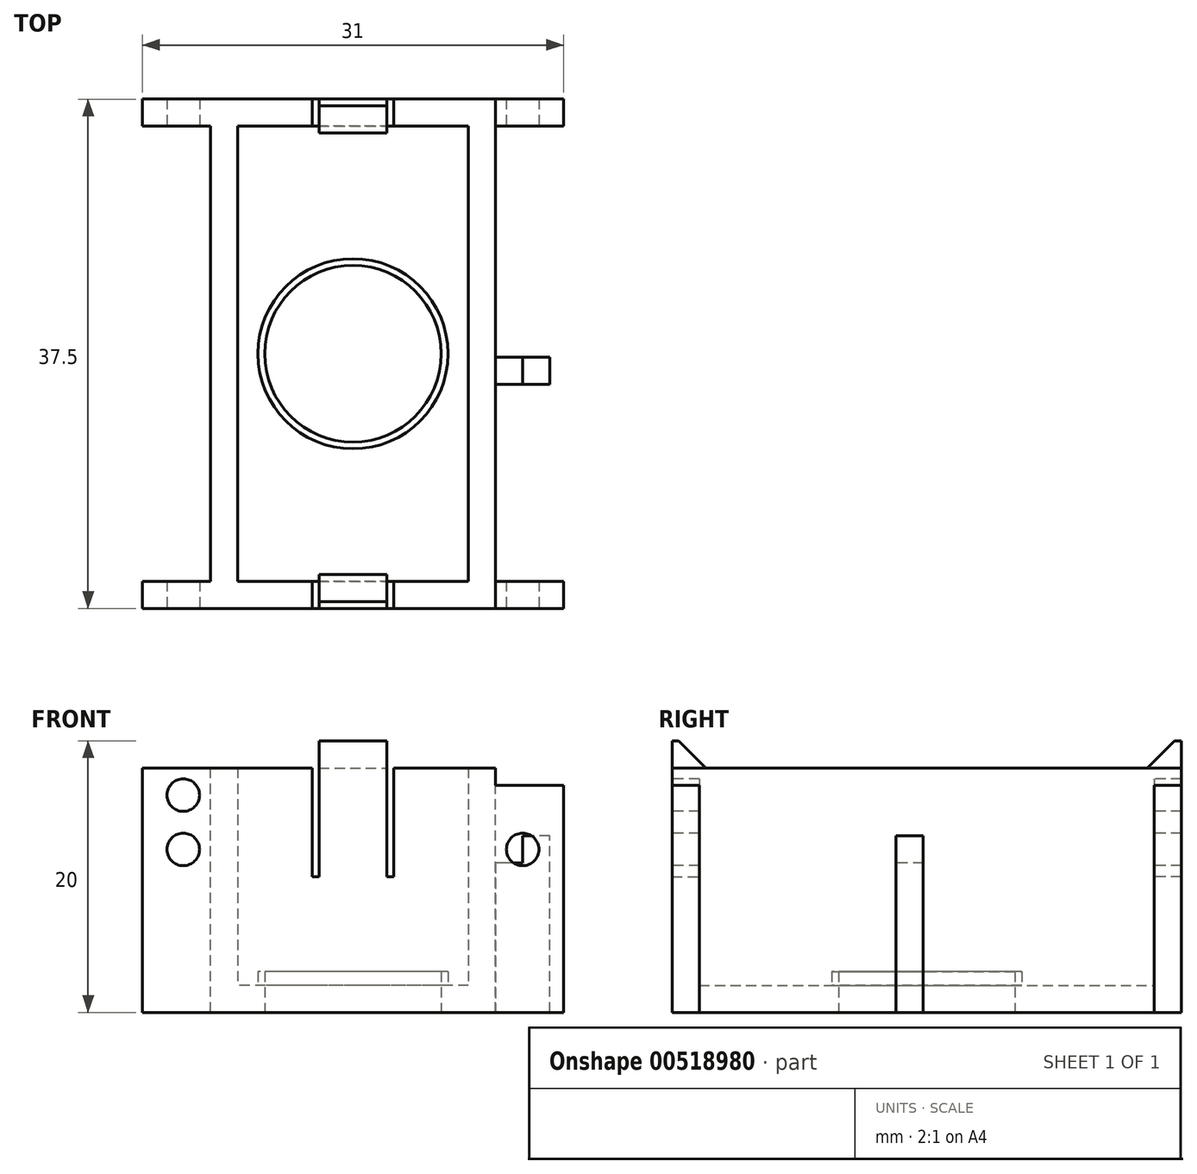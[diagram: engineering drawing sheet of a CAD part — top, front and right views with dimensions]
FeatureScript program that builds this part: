
annotation { "Feature Type Name" : "Feature", "Feature Type Description" : "" }
export const myFeature = defineFeature(function(context is Context, id is Id, definition is map)
    precondition{}
    {
        {
            var Q0;
            Q0=qCreatedBy(makeId("Top.planeOp"),FACE);
            var sketch = newSketch(context, id + "F0", { "sketchPlane" : qUnion([Q0])});
            skLineSegment(sketch, "E0.bottom", {"start": v(-9.66, 7.75) * mm, "end": v(7.34, 7.75) * mm});
            skLineSegment(sketch, "E0.top", {"start": v(-9.66, -25.75) * mm, "end": v(7.34, -25.75) * mm});
            skLineSegment(sketch, "E0.left", {"start": v(-9.66, 7.75) * mm, "end": v(-9.66, -25.75) * mm});
            skLineSegment(sketch, "E0.right", {"start": v(7.34, 7.75) * mm, "end": v(7.34, -25.75) * mm});
            skLineSegment(sketch, "E1.bottom", {"start": v(-11.66, 9.75) * mm, "end": v(9.34, 9.75) * mm});
            skLineSegment(sketch, "E1.top", {"start": v(-11.66, -27.75) * mm, "end": v(9.34, -27.75) * mm});
            skLineSegment(sketch, "E1.left", {"start": v(-11.66, 9.75) * mm, "end": v(-11.66, -27.75) * mm});
            skLineSegment(sketch, "E1.right", {"start": v(9.34, 9.75) * mm, "end": v(9.34, -27.75) * mm});
            skLineSegment(sketch, "E2", {"start": v(7.34, 0) * mm, "end": v(9.34, 0) * mm, "construction": true});
            skLineSegment(sketch, "E3", {"start": v(-9.66, 5.82) * mm, "end": v(-11.66, 5.82) * mm, "construction": true});
            skLineSegment(sketch, "E4", {"start": v(13.26, 7.75) * mm, "end": v(13.26, 9.75) * mm, "construction": true});
            skLineSegment(sketch, "E5", {"start": v(14.78, -25.75) * mm, "end": v(14.78, -27.75) * mm, "construction": true});
            skLineSegment(sketch, "E6.top", {"start": v(-9.66, -1.25) * mm, "end": v(7.34, -1.25) * mm});
            skLineSegment(sketch, "E6.left", {"start": v(-9.66, 7.75) * mm, "end": v(-9.66, -1.25) * mm});
            skLineSegment(sketch, "E6.right", {"start": v(7.34, 7.75) * mm, "end": v(7.34, -1.25) * mm});
            skLineSegment(sketch, "E7.top", {"start": v(-9.66, -16.75) * mm, "end": v(7.34, -16.75) * mm});
            skLineSegment(sketch, "E7.left", {"start": v(-9.66, -25.75) * mm, "end": v(-9.66, -16.75) * mm});
            skLineSegment(sketch, "E7.right", {"start": v(7.34, -25.75) * mm, "end": v(7.34, -16.75) * mm});
            skCircle(sketch, "E8", {"center": v(-1.16, 1.95) * mm, "radius": 5.5 * mm});
            skCircle(sketch, "E9", {"center": v(-1.16, -19.95) * mm, "radius": 5.5 * mm});
            skLineSegment(sketch, "E10", {"start": v(-1.16, 7.75) * mm, "end": v(-1.16, 1.95) * mm, "construction": true});
            skLineSegment(sketch, "E11", {"start": v(-1.16, -25.75) * mm, "end": v(-1.16, -19.95) * mm, "construction": true});
            skLineSegment(sketch, "E12.bottom", {"start": v(-5.16, 9.75) * mm, "end": v(2.84, 9.75) * mm});
            skLineSegment(sketch, "E13.bottom", {"start": v(-5.16, -27.75) * mm, "end": v(2.84, -27.75) * mm});
            skLineSegment(sketch, "E13.left", {"start": v(-5.16, -27.75) * mm, "end": v(-5.16, -35.75) * mm});
            skLineSegment(sketch, "E13.right", {"start": v(2.84, -27.75) * mm, "end": v(2.84, -35.75) * mm});
            skCircle(sketch, "E14", {"center": v(-1.16, 13.5) * mm, "radius": 1.7 * mm});
            skLineSegment(sketch, "E15", {"start": v(-1.16, -31.5) * mm, "end": v(-1.16, -27.75) * mm, "construction": true});
            skLineSegment(sketch, "E16", {"start": v(-1.16, 13.5) * mm, "end": v(-1.16, 9.75) * mm, "construction": true});
            skCircle(sketch, "E17", {"center": v(-1.16, -9) * mm, "radius": 6.5 * mm});
            skPoint(sketch, "E17.centerSnap0", {"position": v(-1.16, -1.25) * mm});
            skLineSegment(sketch, "E18", {"start": v(-1.16, -9) * mm, "end": v(-1.16, 1.95) * mm, "construction": true});
            skLineSegment(sketch, "E19", {"start": v(-1.16, -9) * mm, "end": v(-1.16, -19.95) * mm, "construction": true});
            skCircle(sketch, "E20", {"center": v(-1.16, -9) * mm, "radius": 7 * mm});
            skSolve(sketch);
        }
        {
            var Q0;
            Q0=makeQuery(id+"F0.imprint","IMPRINT",FACE,{"disambiguationData":[TD([[makeQuery(id+"F0.imprint","IMPRINT",EDGE,{"derivedFrom":sQuery(id+"F0.wireOp",EDGE,"E0.left")}),-1.0]])]});
            var Q1;
            Q1=makeQuery(id+"F0.imprint","IMPRINT",FACE,{"disambiguationData":[TD([[makeQuery(id+"F0.imprint","IMPRINT",EDGE,{"derivedFrom":sQuery(id+"F0.wireOp",EDGE,"E0.bottom")}),-1.0]])]});
            var Q2;
            Q2=makeQuery(id+"F0.imprint","IMPRINT",FACE,{"disambiguationData":[TD([[makeQuery(id+"F0.imprint","IMPRINT",EDGE,{"derivedFrom":sQuery(id+"F0.wireOp",EDGE,"E0.top")}),1.0]])]});
            var Q3;
            Q3=makeQuery(id+"F0.imprint","IMPRINT",FACE,{"disambiguationData":[TD([[makeQuery(id+"F0.imprint","IMPRINT",EDGE,{"derivedFrom":sQuery(id+"F0.wireOp",EDGE,"E12.bottom")}),1.0]])]});
            var Q4;
            Q4=makeQuery(id+"F0.imprint","IMPRINT",FACE,{"disambiguationData":[TD([[makeQuery(id+"F0.imprint","IMPRINT",EDGE,{"derivedFrom":sQuery(id+"F0.wireOp",EDGE,"E13.bottom")}),-1.0]])]});
            var Q5;
            {var subQ0=sQuery(id+"F0.wireOp",EDGE,"E9");var subQ1=sQuery(id+"F0.wireOp",EDGE,"E7.top");var subQ2=makeQuery(id+"F0.imprint","INTERSECT",VERTEX,{"disambiguationData":[OD(0.0)],"derivedFrom":[subQ1,subQ0]});Q5=makeQuery(id+"F0.imprint","IMPRINT",FACE,{"disambiguationData":[TD([[makeQuery(id+"F0.imprint","IMPRINT",EDGE,{"disambiguationData":[TD([[subQ2,-1.0]])],"derivedFrom":subQ1}),-1.0]])]});}
            var Q6;
            {var subQ0=sQuery(id+"F0.wireOp",EDGE,"E8");var subQ1=sQuery(id+"F0.wireOp",EDGE,"E6.top");var subQ2=makeQuery(id+"F0.imprint","INTERSECT",VERTEX,{"disambiguationData":[OD(0.0)],"derivedFrom":[subQ1,subQ0]});Q6=makeQuery(id+"F0.imprint","IMPRINT",FACE,{"disambiguationData":[TD([[makeQuery(id+"F0.imprint","IMPRINT",EDGE,{"disambiguationData":[TD([[subQ2,-1.0]])],"derivedFrom":subQ1}),1.0]])]});}
            var Q7;
            {var subQ6=sQuery(id+"F0.wireOp",EDGE,"E0.right");Q7=makeQuery(id+"F0.imprint","IMPRINT",FACE,{"disambiguationData":[TD([[makeQuery(id+"F0.imprint","IMPRINT",EDGE,{"derivedFrom":subQ6}),-1.0]])]});}
            var Q8;
            {var subQ0=sQuery(id+"F0.wireOp",EDGE,"E8");var subQ1=sQuery(id+"F0.wireOp",EDGE,"E6.top");var subQ2=makeQuery(id+"F0.imprint","INTERSECT",VERTEX,{"disambiguationData":[OD(0.0)],"derivedFrom":[subQ1,subQ0]});Q8=makeQuery(id+"F0.imprint","IMPRINT",FACE,{"disambiguationData":[TD([[makeQuery(id+"F0.imprint","IMPRINT",EDGE,{"disambiguationData":[TD([[subQ2,-1.0]])],"derivedFrom":subQ1}),-1.0]])]});}
            var Q9;
            {var subQ1=sQuery(id+"F0.wireOp",EDGE,"E0.left");Q9=makeQuery(id+"F0.imprint","IMPRINT",FACE,{"disambiguationData":[TD([[makeQuery(id+"F0.imprint","IMPRINT",EDGE,{"derivedFrom":subQ1}),1.0]])]});}
            var Q10;
            {var subQ0=sQuery(id+"F0.wireOp",EDGE,"E9");var subQ1=sQuery(id+"F0.wireOp",EDGE,"E7.top");var subQ2=makeQuery(id+"F0.imprint","INTERSECT",VERTEX,{"disambiguationData":[OD(0.0)],"derivedFrom":[subQ1,subQ0]});Q10=makeQuery(id+"F0.imprint","IMPRINT",FACE,{"disambiguationData":[TD([[makeQuery(id+"F0.imprint","IMPRINT",EDGE,{"disambiguationData":[TD([[subQ2,-1.0]])],"derivedFrom":subQ1}),1.0]])]});}
            extrude(context, id + "F1", {"entities" : qUnion([Q0, Q1, Q2, Q3, Q4, Q5, Q6, Q7, Q8, Q9, Q10]), "depth" : 2 * mm, "offsetDistance" : 25 * mm});
        }
        {
            var Q0;
            Q0=makeQuery(id+"F0.imprint","IMPRINT",FACE,{"disambiguationData":[TD([[makeQuery(id+"F0.imprint","IMPRINT",EDGE,{"derivedFrom":sQuery(id+"F0.wireOp",EDGE,"E0.left")}),-1.0]])]});
            extrude(context, id + "F2", {"entities" : qUnion([Q0]), "operationType" : NewBodyOperationType.ADD, "depth" : 9 * mm + 9 * mm, "offsetDistance" : 25 * mm});
        }
        {
            var Q0;
            {var subQ0=sQuery(id+"F0.wireOp",EDGE,"E20");var subQ1=sQuery(id+"F0.wireOp",EDGE,"E8");var subQ2=makeQuery(id+"F0.imprint","INTERSECT",VERTEX,{"disambiguationData":[OD(0.0)],"derivedFrom":[subQ1,subQ0]});Q0=makeQuery(id+"F0.imprint","IMPRINT",FACE,{"disambiguationData":[TD([[makeQuery(id+"F0.imprint","IMPRINT",EDGE,{"disambiguationData":[TD([[subQ2,-1.0]])],"derivedFrom":subQ1}),-1.0]])]});}
            var Q1;
            {var subQ0=sQuery(id+"F0.wireOp",EDGE,"E20");var subQ1=sQuery(id+"F0.wireOp",EDGE,"E8");var subQ2=makeQuery(id+"F0.imprint","INTERSECT",VERTEX,{"disambiguationData":[OD(0.0)],"derivedFrom":[subQ1,subQ0]});Q1=makeQuery(id+"F0.imprint","IMPRINT",FACE,{"disambiguationData":[TD([[makeQuery(id+"F0.imprint","IMPRINT",EDGE,{"disambiguationData":[TD([[subQ2,-1.0]])],"derivedFrom":subQ1}),1.0]])]});}
            var Q2;
            {var subQ0=sQuery(id+"F0.wireOp",EDGE,"E17");var subQ1=sQuery(id+"F0.wireOp",EDGE,"E8");var subQ2=makeQuery(id+"F0.imprint","INTERSECT",VERTEX,{"disambiguationData":[OD(1.0)],"derivedFrom":[subQ1,subQ0]});Q2=makeQuery(id+"F0.imprint","IMPRINT",FACE,{"disambiguationData":[TD([[makeQuery(id+"F0.imprint","IMPRINT",EDGE,{"disambiguationData":[TD([[subQ2,-1.0]])],"derivedFrom":subQ1}),-1.0]])]});}
            var Q3;
            {var subQ0=sQuery(id+"F0.wireOp",EDGE,"E20");var subQ1=sQuery(id+"F0.wireOp",EDGE,"E9");var subQ2=makeQuery(id+"F0.imprint","INTERSECT",VERTEX,{"disambiguationData":[OD(0.0)],"derivedFrom":[subQ1,subQ0]});Q3=makeQuery(id+"F0.imprint","IMPRINT",FACE,{"disambiguationData":[TD([[makeQuery(id+"F0.imprint","IMPRINT",EDGE,{"disambiguationData":[TD([[subQ2,-1.0]])],"derivedFrom":subQ1}),1.0]])]});}
            extrude(context, id + "F3", {"entities" : qUnion([Q0, Q1, Q2, Q3]), "operationType" : NewBodyOperationType.ADD, "depth" : 3 * mm, "offsetDistance" : 25 * mm});
        }
        {
            var Q0;
            {var subQ0=sQuery(id+"F0.wireOp",EDGE,"E1.left");Q0=makeQuery(id+"F2.boolean.opBoolean","MERGE",FACE,{"derivedFrom":[makeQuery(id+"F1.opExtrude","SWEPT_FACE",FACE,{"disambiguationData":[OSD([subQ0])]}),makeQuery(id+"F2.opExtrude","SWEPT_FACE",FACE,{"disambiguationData":[OSD([subQ0])]})]});}
            var sketch = newSketch(context, id + "F4", { "sketchPlane" : qUnion([Q0])});
            skLineSegment(sketch, "E21.bottom", {"start": v(-9.75, 0) * mm, "end": v(-7.75, 0) * mm});
            skLineSegment(sketch, "E21.top", {"start": v(-9.75, 5) * mm, "end": v(-7.75, 5) * mm});
            skLineSegment(sketch, "E21.left", {"start": v(-9.75, 0) * mm, "end": v(-9.75, 5) * mm});
            skLineSegment(sketch, "E21.right", {"start": v(-7.75, 0) * mm, "end": v(-7.75, 5) * mm});
            skLineSegment(sketch, "E22.bottom", {"start": v(27.75, 0) * mm, "end": v(25.75, 0) * mm});
            skLineSegment(sketch, "E22.top", {"start": v(27.75, 5) * mm, "end": v(25.75, 5) * mm});
            skLineSegment(sketch, "E22.left", {"start": v(27.75, 0) * mm, "end": v(27.75, 5) * mm});
            skLineSegment(sketch, "E22.right", {"start": v(25.75, 0) * mm, "end": v(25.75, 5) * mm});
            skLineSegment(sketch, "E23.bottom", {"start": v(-9.75, 18) * mm, "end": v(-7.75, 18) * mm});
            skLineSegment(sketch, "E23.left", {"start": v(-9.75, 18) * mm, "end": v(-9.75, 5) * mm});
            skLineSegment(sketch, "E23.right", {"start": v(-7.75, 18) * mm, "end": v(-7.75, 5) * mm});
            skLineSegment(sketch, "E24.bottom", {"start": v(25.75, 5) * mm, "end": v(27.75, 5) * mm});
            skLineSegment(sketch, "E24.top", {"start": v(25.75, 18) * mm, "end": v(27.75, 18) * mm});
            skLineSegment(sketch, "E24.left", {"start": v(25.75, 5) * mm, "end": v(25.75, 18) * mm});
            skLineSegment(sketch, "E24.right", {"start": v(27.75, 5) * mm, "end": v(27.75, 18) * mm});
            skSolve(sketch);
        }
        {
            var Q0;
            Q0=qSketchRegion(id+"F4",true);
            extrude(context, id + "F5", {"entities" : qUnion([Q0]), "operationType" : NewBodyOperationType.ADD, "depth" : 5 * mm, "offsetDistance" : 25 * mm});
        }
        {
            var Q0;
            {var subQ0=sQuery(id+"F0.wireOp",EDGE,"E1.right");Q0=makeQuery(id+"F2.boolean.opBoolean","MERGE",FACE,{"derivedFrom":[makeQuery(id+"F1.opExtrude","SWEPT_FACE",FACE,{"disambiguationData":[OSD([subQ0])]}),makeQuery(id+"F2.opExtrude","SWEPT_FACE",FACE,{"disambiguationData":[OSD([subQ0])]})]});}
            var sketch = newSketch(context, id + "F6", { "sketchPlane" : qUnion([Q0])});
            skLineSegment(sketch, "E25.bottom", {"start": v(-27.75, 0) * mm, "end": v(-25.75, 0) * mm});
            skLineSegment(sketch, "E25.top", {"start": v(-27.75, 16.72) * mm, "end": v(-25.75, 16.72) * mm});
            skLineSegment(sketch, "E25.left", {"start": v(-27.75, 0) * mm, "end": v(-27.75, 16.72) * mm});
            skLineSegment(sketch, "E25.right", {"start": v(-25.75, 0) * mm, "end": v(-25.75, 16.72) * mm});
            skLineSegment(sketch, "E26.bottom", {"start": v(9.75, 0) * mm, "end": v(7.75, 0) * mm});
            skLineSegment(sketch, "E26.top", {"start": v(9.75, 16.72) * mm, "end": v(7.75, 16.72) * mm});
            skLineSegment(sketch, "E26.left", {"start": v(9.75, 0) * mm, "end": v(9.75, 16.72) * mm});
            skLineSegment(sketch, "E26.right", {"start": v(7.75, 0) * mm, "end": v(7.75, 16.72) * mm});
            skSolve(sketch);
        }
        {
            var Q0;
            Q0=qSketchRegion(id+"F6",true);
            extrude(context, id + "F7", {"entities" : qUnion([Q0]), "operationType" : NewBodyOperationType.ADD, "depth" : 5 * mm, "offsetDistance" : 25 * mm});
        }
        {
            var Q0;
            {var subQ0=sQuery(id+"F0.wireOp",EDGE,"E13.bottom");var subQ1=sQuery(id+"F0.wireOp",EDGE,"E1.top");Q0=makeQuery(id+"F7.boolean.opBoolean","MERGE",FACE,{"derivedFrom":[makeQuery(id+"F5.boolean.opBoolean","MERGE",FACE,{"derivedFrom":[makeQuery(id+"F2.boolean.opBoolean","MERGE",FACE,{"derivedFrom":[makeQuery(id+"F1.opExtrude","SWEPT_FACE",FACE,{"disambiguationData":[OSD([subQ1,subQ0])]}),makeQuery(id+"F2.opExtrude","SWEPT_FACE",FACE,{"disambiguationData":[OSD([subQ1,subQ0])]})]}),makeQuery(id+"F5.opExtrude","SWEPT_FACE",FACE,{"disambiguationData":[OSD([sQuery(id+"F4.wireOp",EDGE,"E22.left")])]})]}),makeQuery(id+"F7.opExtrude","SWEPT_FACE",FACE,{"disambiguationData":[OSD([sQuery(id+"F6.wireOp",EDGE,"E25.left")])]})]});}
            var sketch = newSketch(context, id + "F8", { "sketchPlane" : qUnion([Q0])});
            skCircle(sketch, "E27", {"center": v(-13.66, 12) * mm, "radius": 1.2 * mm});
            skPoint(sketch, "E27.centerSnap0", {"position": v(-13.66, 5) * mm});
            skCircle(sketch, "E28", {"center": v(11.34, 12) * mm, "radius": 1.2 * mm});
            skLineSegment(sketch, "E29", {"start": v(-13.66, 12) * mm, "end": v(-16.66, 12) * mm, "construction": true});
            skLineSegment(sketch, "E30", {"start": v(11.34, 12) * mm, "end": v(14.34, 12) * mm, "construction": true});
            skCircle(sketch, "E31", {"center": v(-13.66, 16) * mm, "radius": 1.2 * mm});
            skSolve(sketch);
        }
        {
            var Q0;
            Q0=qSketchRegion(id+"F8",true);
            extrude(context, id + "F9", {"entities" : qUnion([Q0]), "operationType" : NewBodyOperationType.REMOVE, "oppositeDirection" : true, "depth" : 40 * mm, "offsetDistance" : 25 * mm});
        }
        {
            var Q0;
            {var subQ0=sQuery(id+"F0.wireOp",EDGE,"E12.bottom");var subQ1=sQuery(id+"F0.wireOp",EDGE,"E1.bottom");Q0=makeQuery(id+"F7.boolean.opBoolean","MERGE",FACE,{"derivedFrom":[makeQuery(id+"F5.boolean.opBoolean","MERGE",FACE,{"derivedFrom":[makeQuery(id+"F2.boolean.opBoolean","MERGE",FACE,{"derivedFrom":[makeQuery(id+"F1.opExtrude","SWEPT_FACE",FACE,{"disambiguationData":[OSD([subQ1,subQ0])]}),makeQuery(id+"F2.opExtrude","SWEPT_FACE",FACE,{"disambiguationData":[OSD([subQ1,subQ0])]})]}),makeQuery(id+"F5.opExtrude","SWEPT_FACE",FACE,{"disambiguationData":[OSD([sQuery(id+"F4.wireOp",EDGE,"E21.left")])]})]}),makeQuery(id+"F7.opExtrude","SWEPT_FACE",FACE,{"disambiguationData":[OSD([sQuery(id+"F6.wireOp",EDGE,"E26.left")])]})]});}
            cPlane(context, id + "F10", {"entities" : qUnion([Q0]), "cplaneType" : CPlaneType.OFFSET, "offset" : 20 * mm, "oppositeDirection" : true, "width" : 150 * mm, "height" : 150 * mm});
        }
        {
            var Q0;
            Q0=qCreatedBy(id+"F10.planeOp",FACE);
            var sketch = newSketch(context, id + "F11", { "sketchPlane" : qUnion([Q0])});
            skLineSegment(sketch, "E32", {"start": v(-13.34, 0) * mm, "end": v(-13.34, 13) * mm});
            skLineSegment(sketch, "E33", {"start": v(-13.34, 13) * mm, "end": v(-11.34, 13) * mm});
            skLineSegment(sketch, "E34", {"start": v(-11.34, 13) * mm, "end": v(-11.34, 11) * mm});
            skLineSegment(sketch, "E35", {"start": v(-11.34, 11) * mm, "end": v(-9.34, 11) * mm});
            skLineSegment(sketch, "E36", {"start": v(-9.34, 11) * mm, "end": v(-9.34, 0) * mm});
            skLineSegment(sketch, "E37", {"start": v(-9.34, 0) * mm, "end": v(-13.34, 0) * mm});
            skSolve(sketch);
        }
        {
            var Q0;
            Q0=qSketchRegion(id+"F11",true);
            extrude(context, id + "F12", {"entities" : qUnion([Q0]), "operationType" : NewBodyOperationType.ADD, "depth" : 2 * mm, "offsetDistance" : 25 * mm, "symmetric" : true});
        }
        {
            var Q0;
            Q0=makeQuery(id+"F2.opExtrude","CAP_FACE",FACE,{"disambiguationData":[OSD([sQuery(id+"F0.wireOp",EDGE,"E0.left"),sQuery(id+"F0.wireOp",EDGE,"E0.right"),sQuery(id+"F0.wireOp",EDGE,"E1.bottom"),sQuery(id+"F0.wireOp",EDGE,"E1.top"),sQuery(id+"F0.wireOp",EDGE,"E1.left"),sQuery(id+"F0.wireOp",EDGE,"E1.right"),sQuery(id+"F0.wireOp",EDGE,"E0.bottom"),sQuery(id+"F0.wireOp",EDGE,"E6.left"),sQuery(id+"F0.wireOp",EDGE,"E6.right"),sQuery(id+"F0.wireOp",EDGE,"E0.top"),sQuery(id+"F0.wireOp",EDGE,"E7.left"),sQuery(id+"F0.wireOp",EDGE,"E7.right"),sQuery(id+"F0.wireOp",EDGE,"E12.bottom"),sQuery(id+"F0.wireOp",EDGE,"E13.bottom")])],"isStart":false});
            var sketch = newSketch(context, id + "F13", { "sketchPlane" : qUnion([Q0])});
            skLineSegment(sketch, "E38.bottom", {"start": v(-3.66, 9.75) * mm, "end": v(1.34, 9.75) * mm});
            skLineSegment(sketch, "E38.top", {"start": v(-3.66, 7.25) * mm, "end": v(1.34, 7.25) * mm});
            skLineSegment(sketch, "E38.left", {"start": v(-3.66, 9.75) * mm, "end": v(-3.66, 7.25) * mm});
            skLineSegment(sketch, "E38.right", {"start": v(1.34, 9.75) * mm, "end": v(1.34, 7.25) * mm});
            skLineSegment(sketch, "E39.bottom", {"start": v(-3.66, -27.75) * mm, "end": v(1.34, -27.75) * mm});
            skLineSegment(sketch, "E39.top", {"start": v(-3.66, -25.25) * mm, "end": v(1.34, -25.25) * mm});
            skLineSegment(sketch, "E39.left", {"start": v(-3.66, -27.75) * mm, "end": v(-3.66, -25.25) * mm});
            skLineSegment(sketch, "E39.right", {"start": v(1.34, -27.75) * mm, "end": v(1.34, -25.25) * mm});
            skLineSegment(sketch, "E40", {"start": v(1.34, -25.43) * mm, "end": v(7.34, -25.43) * mm, "construction": true});
            skLineSegment(sketch, "E41", {"start": v(-3.66, -25.4) * mm, "end": v(-9.66, -25.4) * mm, "construction": true});
            skLineSegment(sketch, "E42.bottom", {"start": v(-3.66, 9.75) * mm, "end": v(-4.16, 9.75) * mm});
            skLineSegment(sketch, "E42.top", {"start": v(-3.66, 7.75) * mm, "end": v(-4.16, 7.75) * mm});
            skLineSegment(sketch, "E42.left", {"start": v(-3.66, 9.75) * mm, "end": v(-3.66, 7.75) * mm});
            skLineSegment(sketch, "E42.right", {"start": v(-4.16, 9.75) * mm, "end": v(-4.16, 7.75) * mm});
            skLineSegment(sketch, "E43.bottom", {"start": v(1.34, 9.75) * mm, "end": v(1.84, 9.75) * mm});
            skLineSegment(sketch, "E43.top", {"start": v(1.34, 7.75) * mm, "end": v(1.84, 7.75) * mm});
            skLineSegment(sketch, "E43.left", {"start": v(1.34, 9.75) * mm, "end": v(1.34, 7.75) * mm});
            skLineSegment(sketch, "E43.right", {"start": v(1.84, 9.75) * mm, "end": v(1.84, 7.75) * mm});
            skLineSegment(sketch, "E44.bottom", {"start": v(1.34, -27.75) * mm, "end": v(1.84, -27.75) * mm});
            skLineSegment(sketch, "E44.top", {"start": v(1.34, -25.75) * mm, "end": v(1.84, -25.75) * mm});
            skLineSegment(sketch, "E44.left", {"start": v(1.34, -27.75) * mm, "end": v(1.34, -25.75) * mm});
            skLineSegment(sketch, "E44.right", {"start": v(1.84, -27.75) * mm, "end": v(1.84, -25.75) * mm});
            skLineSegment(sketch, "E45.bottom", {"start": v(-3.66, -27.75) * mm, "end": v(-4.16, -27.75) * mm});
            skLineSegment(sketch, "E45.top", {"start": v(-3.66, -25.75) * mm, "end": v(-4.16, -25.75) * mm});
            skLineSegment(sketch, "E45.left", {"start": v(-3.66, -27.75) * mm, "end": v(-3.66, -25.75) * mm});
            skLineSegment(sketch, "E45.right", {"start": v(-4.16, -27.75) * mm, "end": v(-4.16, -25.75) * mm});
            skSolve(sketch);
        }
        {
            var Q0;
            Q0=makeQuery(id+"F13.imprint","IMPRINT",FACE,{"disambiguationData":[TD([[makeQuery(id+"F13.imprint","IMPRINT",EDGE,{"derivedFrom":sQuery(id+"F13.wireOp",EDGE,"E39.bottom")}),1.0]])]});
            var Q1;
            Q1=makeQuery(id+"F13.imprint","IMPRINT",FACE,{"disambiguationData":[TD([[makeQuery(id+"F13.imprint","IMPRINT",EDGE,{"derivedFrom":sQuery(id+"F13.wireOp",EDGE,"E39.top")}),-1.0]])]});
            var Q2;
            Q2=makeQuery(id+"F13.imprint","IMPRINT",FACE,{"disambiguationData":[TD([[makeQuery(id+"F13.imprint","IMPRINT",EDGE,{"derivedFrom":sQuery(id+"F13.wireOp",EDGE,"E38.bottom")}),-1.0]])]});
            var Q3;
            Q3=makeQuery(id+"F13.imprint","IMPRINT",FACE,{"disambiguationData":[TD([[makeQuery(id+"F13.imprint","IMPRINT",EDGE,{"derivedFrom":sQuery(id+"F13.wireOp",EDGE,"E38.top")}),1.0]])]});
            extrude(context, id + "F14", {"entities" : qUnion([Q0, Q1, Q2, Q3]), "operationType" : NewBodyOperationType.ADD, "depth" : 2 * mm, "offsetDistance" : 25 * mm});
        }
        {
            var Q0;
            Q0=makeQuery(id+"F14.opExtrude","CAP_EDGE",EDGE,{"disambiguationData":[OSD([sQuery(id+"F13.wireOp",EDGE,"E39.top")])],"isStart":false});
            var Q1;
            Q1=makeQuery(id+"F14.opExtrude","CAP_EDGE",EDGE,{"disambiguationData":[OSD([sQuery(id+"F13.wireOp",EDGE,"E38.top")])],"isStart":false});
            chamfer(context, id + "F15", {"entities" : qUnion([Q0, Q1]), "width" : 2 * mm, "tangentPropagation" : true});
        }
        {
            var Q0;
            Q0=makeQuery(id+"F13.imprint","IMPRINT",FACE,{"disambiguationData":[TD([[makeQuery(id+"F13.imprint","IMPRINT",EDGE,{"derivedFrom":sQuery(id+"F13.wireOp",EDGE,"E45.bottom")}),1.0]])]});
            var Q1;
            Q1=makeQuery(id+"F13.imprint","IMPRINT",FACE,{"disambiguationData":[TD([[makeQuery(id+"F13.imprint","IMPRINT",EDGE,{"derivedFrom":sQuery(id+"F13.wireOp",EDGE,"E44.bottom")}),1.0]])]});
            var Q2;
            Q2=makeQuery(id+"F13.imprint","IMPRINT",FACE,{"disambiguationData":[TD([[makeQuery(id+"F13.imprint","IMPRINT",EDGE,{"derivedFrom":sQuery(id+"F13.wireOp",EDGE,"E43.bottom")}),-1.0]])]});
            var Q3;
            Q3=makeQuery(id+"F13.imprint","IMPRINT",FACE,{"disambiguationData":[TD([[makeQuery(id+"F13.imprint","IMPRINT",EDGE,{"derivedFrom":sQuery(id+"F13.wireOp",EDGE,"E42.bottom")}),-1.0]])]});
            extrude(context, id + "F16", {"entities" : qUnion([Q0, Q1, Q2, Q3]), "operationType" : NewBodyOperationType.REMOVE, "oppositeDirection" : true, "depth" : 8 * mm, "offsetDistance" : 25 * mm});
        }
    });
